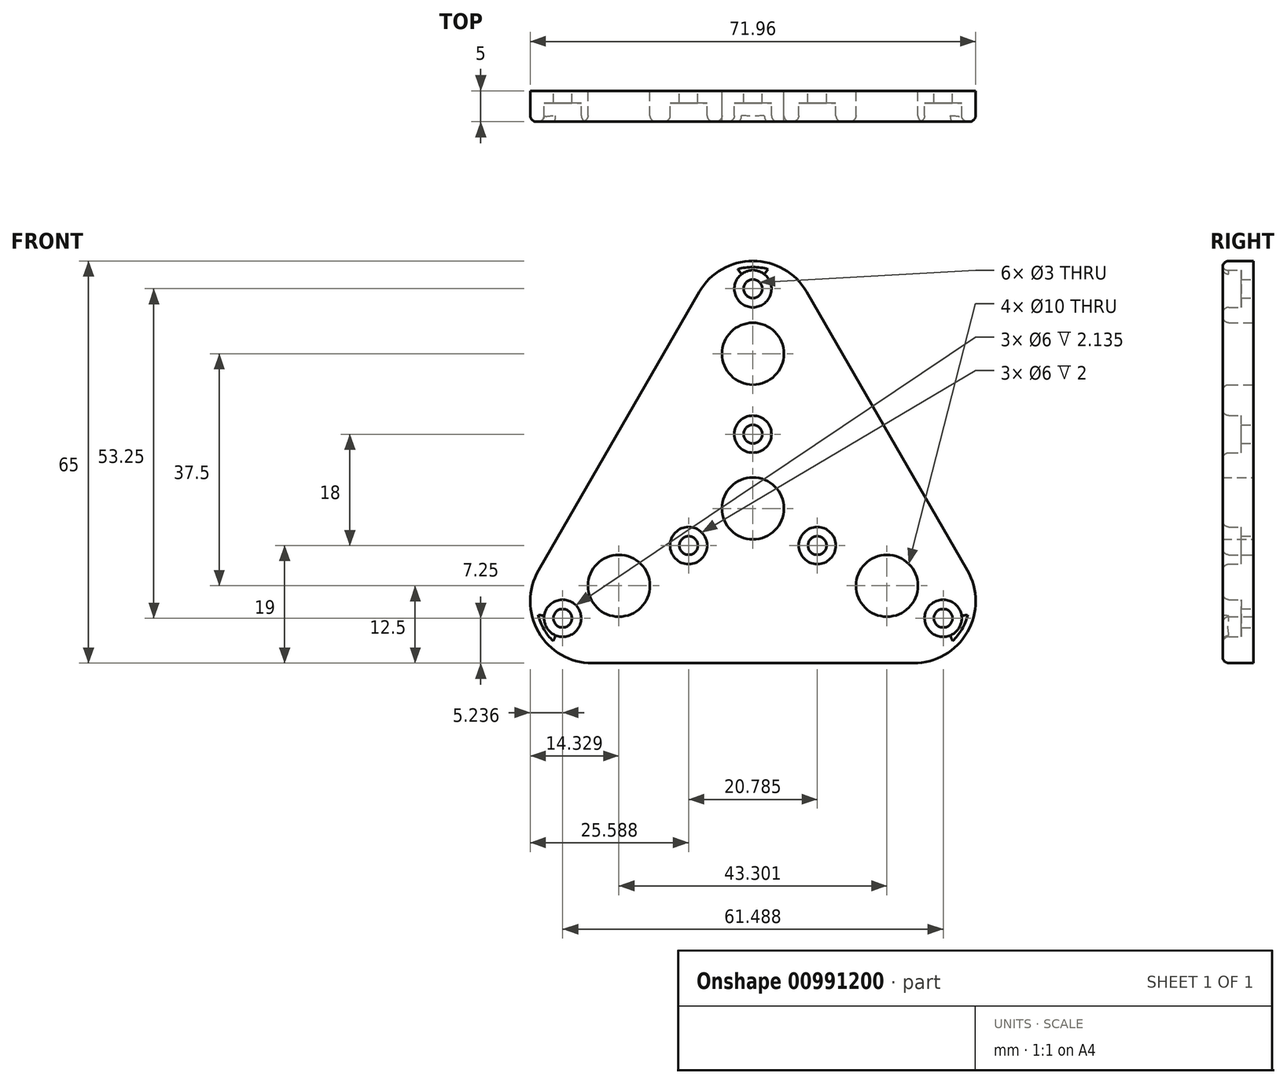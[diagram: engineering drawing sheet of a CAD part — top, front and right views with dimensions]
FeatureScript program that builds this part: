
annotation { "Feature Type Name" : "Feature", "Feature Type Description" : "" }
export const myFeature = defineFeature(function(context is Context, id is Id, definition is map)
    precondition{}
    {
        {
            var Q0;
            Q0=qCreatedBy(makeId("Front.planeOp"),FACE);
            var sketch = newSketch(context, id + "F0", { "sketchPlane" : qUnion([Q0])});
            skCircle(sketch, "E0", {"center": v(0, 0) * mm, "radius": 25 * mm, "construction": true});
            skLineSegment(sketch, "E1.0", {"start": v(25.98, -25) * mm, "end": v(-25.98, -25) * mm});
            skLineSegment(sketch, "E1.1", {"start": v(-34.64, -10) * mm, "end": v(-8.66, 35) * mm});
            skLineSegment(sketch, "E1.2", {"start": v(8.66, 35) * mm, "end": v(34.64, -10) * mm});
            skPoint(sketch, "E1.0.midPoint", {"position": v(0, -25) * mm});
            skPoint(sketch, "E2.visualSharp", {"position": v(-43.3, -25) * mm});
            skArc(sketch, "E2.filletArc", {"start": v(-34.64, -10) * mm, "mid": v(-34.64, -20) * mm, "end": v(-25.98, -25) * mm});
            skPoint(sketch, "E3.visualSharp", {"position": v(43.3, -25) * mm});
            skArc(sketch, "E3.filletArc", {"start": v(25.98, -25) * mm, "mid": v(34.64, -20) * mm, "end": v(34.64, -10) * mm});
            skPoint(sketch, "E4.visualSharp", {"position": v(0, 50) * mm});
            skArc(sketch, "E4.filletArc", {"start": v(8.66, 35) * mm, "mid": v(0, 40) * mm, "end": v(-8.66, 35) * mm});
            skLineSegment(sketch, "E5", {"start": v(-34.64, -20) * mm, "end": v(0, 0) * mm, "construction": true});
            skLineSegment(sketch, "E6", {"start": v(0, 0) * mm, "end": v(0, 40) * mm, "construction": true});
            skCircle(sketch, "E7", {"center": v(0, 25) * mm, "radius": 5 * mm});
            skCircle(sketch, "E8", {"center": v(21.65, -12.5) * mm, "radius": 5 * mm});
            skCircle(sketch, "E9", {"center": v(-21.65, -12.5) * mm, "radius": 5 * mm});
            skCircle(sketch, "E10", {"center": v(0, 0) * mm, "radius": 5 * mm});
            skCircle(sketch, "E11", {"center": v(0, 12) * mm, "radius": 3 * mm});
            skCircle(sketch, "E12", {"center": v(10.4, -6) * mm, "radius": 3 * mm});
            skCircle(sketch, "E13", {"center": v(-10.4, -6) * mm, "radius": 3 * mm});
            skCircle(sketch, "E14", {"center": v(30.74, -17.75) * mm, "radius": 3 * mm});
            skCircle(sketch, "E15", {"center": v(0, 35.5) * mm, "radius": 3 * mm});
            skCircle(sketch, "E16", {"center": v(-30.74, -17.75) * mm, "radius": 3 * mm});
            skLineSegment(sketch, "E17", {"start": v(0, 0) * mm, "end": v(34.64, -20) * mm, "construction": true});
            skCircle(sketch, "E18", {"center": v(-30.74, -17.75) * mm, "radius": 1.5 * mm});
            skCircle(sketch, "E19", {"center": v(-10.4, -6) * mm, "radius": 1.5 * mm});
            skCircle(sketch, "E20", {"center": v(10.4, -6) * mm, "radius": 1.5 * mm});
            skCircle(sketch, "E21", {"center": v(30.74, -17.75) * mm, "radius": 1.5 * mm});
            skCircle(sketch, "E22", {"center": v(0, 12) * mm, "radius": 1.5 * mm});
            skCircle(sketch, "E23", {"center": v(0, 35.5) * mm, "radius": 1.5 * mm});
            skSolve(sketch);
        }
        {
            var Q0;
            Q0=qSketchRegion(id+"F0",true);
            extrude(context, id + "F1", {"entities" : qUnion([Q0]), "depth" : 5 * mm, "offsetDistance" : 25 * mm});
        }
        {
            var Q0;
            Q0=makeQuery(id+"F0.imprint","IMPRINT",FACE,{"disambiguationData":[TD([[makeQuery(id+"F0.imprint","IMPRINT",EDGE,{"derivedFrom":sQuery(id+"F0.wireOp",EDGE,"E16")}),1.0]])]});
            var Q1;
            Q1=makeQuery(id+"F0.imprint","IMPRINT",FACE,{"disambiguationData":[TD([[makeQuery(id+"F0.imprint","IMPRINT",EDGE,{"derivedFrom":sQuery(id+"F0.wireOp",EDGE,"E13")}),1.0]])]});
            var Q2;
            Q2=makeQuery(id+"F0.imprint","IMPRINT",FACE,{"disambiguationData":[TD([[makeQuery(id+"F0.imprint","IMPRINT",EDGE,{"derivedFrom":sQuery(id+"F0.wireOp",EDGE,"E12")}),1.0]])]});
            var Q3;
            Q3=makeQuery(id+"F0.imprint","IMPRINT",FACE,{"disambiguationData":[TD([[makeQuery(id+"F0.imprint","IMPRINT",EDGE,{"derivedFrom":sQuery(id+"F0.wireOp",EDGE,"E14")}),1.0]])]});
            var Q4;
            Q4=makeQuery(id+"F0.imprint","IMPRINT",FACE,{"disambiguationData":[TD([[makeQuery(id+"F0.imprint","IMPRINT",EDGE,{"derivedFrom":sQuery(id+"F0.wireOp",EDGE,"E11")}),1.0]])]});
            var Q5;
            Q5=makeQuery(id+"F0.imprint","IMPRINT",FACE,{"disambiguationData":[TD([[makeQuery(id+"F0.imprint","IMPRINT",EDGE,{"derivedFrom":sQuery(id+"F0.wireOp",EDGE,"E15")}),1.0]])]});
            extrude(context, id + "F2", {"entities" : qUnion([Q0, Q1, Q2, Q3, Q4, Q5]), "operationType" : NewBodyOperationType.ADD, "depth" : 2 * mm, "offsetDistance" : 25 * mm});
        }
        {
            var Q0;
            Q0=makeQuery(id+"F1.opExtrude","CAP_EDGE",EDGE,{"disambiguationData":[OSD([sQuery(id+"F0.wireOp",EDGE,"E1.1")])],"isStart":false});
            var Q1;
            Q1=makeQuery(id+"F1.opExtrude","CAP_EDGE",EDGE,{"disambiguationData":[OSD([sQuery(id+"F0.wireOp",EDGE,"E4.filletArc")])],"isStart":false});
            var Q2;
            Q2=makeQuery(id+"F1.opExtrude","CAP_EDGE",EDGE,{"disambiguationData":[OSD([sQuery(id+"F0.wireOp",EDGE,"E1.2")])],"isStart":false});
            var Q3;
            Q3=makeQuery(id+"F1.opExtrude","CAP_EDGE",EDGE,{"disambiguationData":[OSD([sQuery(id+"F0.wireOp",EDGE,"E3.filletArc")])],"isStart":false});
            var Q4;
            Q4=makeQuery(id+"F1.opExtrude","CAP_EDGE",EDGE,{"disambiguationData":[OSD([sQuery(id+"F0.wireOp",EDGE,"E1.0")])],"isStart":false});
            var Q5;
            Q5=makeQuery(id+"F1.opExtrude","CAP_EDGE",EDGE,{"disambiguationData":[OSD([sQuery(id+"F0.wireOp",EDGE,"E2.filletArc")])],"isStart":false});
            fillet(context, id + "F3", {"entities" : qUnion([Q0, Q1, Q2, Q3, Q4, Q5]), "radius" : 1 * mm, "tangentPropagation" : true, "allowEdgeOverflow" : false});
        }
        {
            var Q0;
            Q0=makeQuery(id+"F1.opExtrude","CAP_EDGE",EDGE,{"disambiguationData":[OSD([sQuery(id+"F0.wireOp",EDGE,"E11")])],"isStart":false});
            var Q1;
            Q1=makeQuery(id+"F1.opExtrude","CAP_EDGE",EDGE,{"disambiguationData":[OSD([sQuery(id+"F0.wireOp",EDGE,"E12")])],"isStart":false});
            var Q2;
            Q2=makeQuery(id+"F1.opExtrude","CAP_EDGE",EDGE,{"disambiguationData":[OSD([sQuery(id+"F0.wireOp",EDGE,"E13")])],"isStart":false});
            var Q3;
            Q3=makeQuery(id+"F1.opExtrude","CAP_EDGE",EDGE,{"disambiguationData":[OSD([sQuery(id+"F0.wireOp",EDGE,"E7")])],"isStart":false});
            var Q4;
            Q4=makeQuery(id+"F1.opExtrude","CAP_EDGE",EDGE,{"disambiguationData":[OSD([sQuery(id+"F0.wireOp",EDGE,"E8")])],"isStart":false});
            var Q5;
            Q5=makeQuery(id+"F1.opExtrude","CAP_EDGE",EDGE,{"disambiguationData":[OSD([sQuery(id+"F0.wireOp",EDGE,"E9")])],"isStart":false});
            var Q6;
            Q6=makeQuery(id+"F1.opExtrude","CAP_EDGE",EDGE,{"disambiguationData":[OSD([sQuery(id+"F0.wireOp",EDGE,"E14")])],"isStart":false});
            var Q7;
            Q7=makeQuery(id+"F1.opExtrude","CAP_EDGE",EDGE,{"disambiguationData":[OSD([sQuery(id+"F0.wireOp",EDGE,"E16")])],"isStart":false});
            var Q8;
            Q8=makeQuery(id+"F1.opExtrude","CAP_EDGE",EDGE,{"disambiguationData":[OSD([sQuery(id+"F0.wireOp",EDGE,"E15")])],"isStart":false});
            fillet(context, id + "F4", {"entities" : qUnion([Q0, Q1, Q2, Q3, Q4, Q5, Q6, Q7, Q8]), "radius" : 1 * mm, "tangentPropagation" : true, "allowEdgeOverflow" : false});
        }
    });
